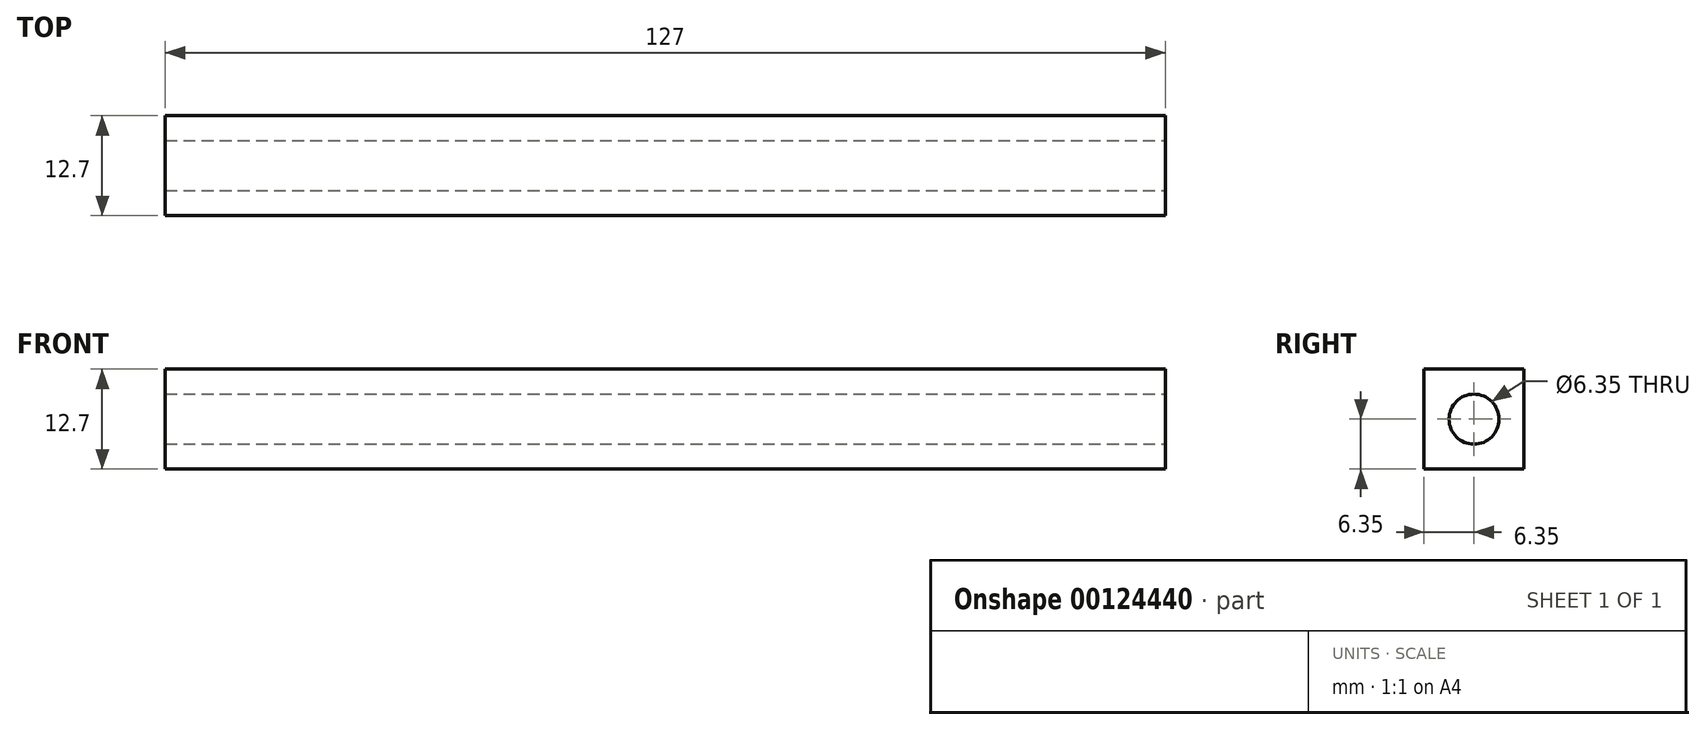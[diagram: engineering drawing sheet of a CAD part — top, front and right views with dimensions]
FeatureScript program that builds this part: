
annotation { "Feature Type Name" : "Feature", "Feature Type Description" : "" }
export const myFeature = defineFeature(function(context is Context, id is Id, definition is map)
    precondition{}
    {
        {
            var Q0;
            Q0=qCreatedBy(makeId("Top.planeOp"),FACE);
            var sketch = newSketch(context, id + "F0", { "sketchPlane" : qUnion([Q0])});
            skLineSegment(sketch, "E0.bottom", {"start": v(0, 0) * mm, "end": v(-76.2, 0) * mm});
            skLineSegment(sketch, "E0.top", {"start": v(0, -12.7) * mm, "end": v(-76.2, -12.7) * mm});
            skLineSegment(sketch, "E0.left", {"start": v(0, 0) * mm, "end": v(0, -12.7) * mm});
            skLineSegment(sketch, "E0.right", {"start": v(-76.2, 0) * mm, "end": v(-76.2, -12.7) * mm});
            skSolve(sketch);
        }
        {
            var Q0;
            Q0=makeQuery(id+"F0.imprint","IMPRINT",FACE,{"disambiguationData":[TD([[makeQuery(id+"F0.imprint","IMPRINT",EDGE,{"derivedFrom":sQuery(id+"F0.wireOp",EDGE,"E0.bottom")}),1.0]])]});
            extrude(context, id + "F1", {"entities" : qUnion([Q0]), "oppositeDirection" : true, "depth" : 12.7 * mm});
        }
        {
            var Q0;
            Q0=makeQuery(id+"F1.opExtrude","SWEPT_FACE",FACE,{"disambiguationData":[OSD([sQuery(id+"F0.wireOp",EDGE,"E0.left")])]});
            var sketch = newSketch(context, id + "F2", { "sketchPlane" : qUnion([Q0])});
            skLineSegment(sketch, "E1", {"start": v(0, -12.7) * mm, "end": v(0, 0) * mm});
            skCircle(sketch, "E2", {"center": v(-6.35, -6.35) * mm, "radius": 3.18 * mm});
            skSolve(sketch);
        }
        {
            var Q0;
            Q0=makeQuery(id+"F2.imprint","IMPRINT",FACE,{"disambiguationData":[TD([[makeQuery(id+"F2.imprint","IMPRINT",EDGE,{"derivedFrom":sQuery(id+"F2.wireOp",EDGE,"E2")}),1.0]])]});
            var Q1;
            Q1=sQuery(id+"F2.wireOp",EDGE,"E2");
            extrude(context, id + "F3", {"entities" : qUnion([Q0]), "operationType" : NewBodyOperationType.REMOVE, "surfaceEntities" : qUnion([Q1]), "oppositeDirection" : true, "depth" : 85.28 * mm});
        }
        {
            var Q0;
            Q0=makeQuery(id+"F1.opExtrude","SWEPT_FACE",FACE,{"disambiguationData":[OSD([sQuery(id+"F0.wireOp",EDGE,"E0.left")])]});
            extrude(context, id + "F4", {"entities" : qUnion([Q0]), "operationType" : NewBodyOperationType.ADD, "depth" : 25.4 * mm});
        }
        {
            var Q0;
            Q0=makeQuery(id+"F1.opExtrude","SWEPT_FACE",FACE,{"disambiguationData":[OSD([sQuery(id+"F0.wireOp",EDGE,"E0.right")])]});
            extrude(context, id + "F5", {"entities" : qUnion([Q0]), "operationType" : NewBodyOperationType.ADD, "depth" : 25.4 * mm});
        }
    });
